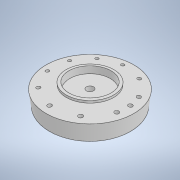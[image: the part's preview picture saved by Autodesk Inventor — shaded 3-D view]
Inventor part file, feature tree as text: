
AUTODESK INVENTOR PART (.ipt)
format: ipt  version: 2022 (Build 260153000, 153)  size: 145,920 bytes
history: native  units: mm
features: extrude x4, sketch x3
ambient origin geometry x8: Origin, YZ Plane, XZ Plane, XY Plane, X Axis, Y Axis, Z Axis, Center Point
bodies: Body1 (feature_tree)
feature tree (7):
  sketch  "Sketch3"  dims[d10=10.0mm d11=0.0mm d12=1.5mm d13=0.0mm]
  extrude  "Extrusion4"  Depth=1.5mm TaperAngle=0.0deg
  extrude  "Extrusion5"  Depth=5.0mm TaperAngle=0.0deg
  extrude  "Extrusion7"  Depth=5.0mm TaperAngle=0.0deg
  extrude  "Extrusion8"  [1 undecoded]
  sketch  "Sketch4"  dims[d16=0.1mm d17=5.0mm d18=0.0mm]
  sketch  "Sketch5"  dims[d19=5.1mm d20=5.0mm d21=0.0mm]
note: 1 required parameter value undecoded (feature->parameter linkage not recoverable at this tier; creation-order binding heuristic only, values carry confidence <= 0.55)
